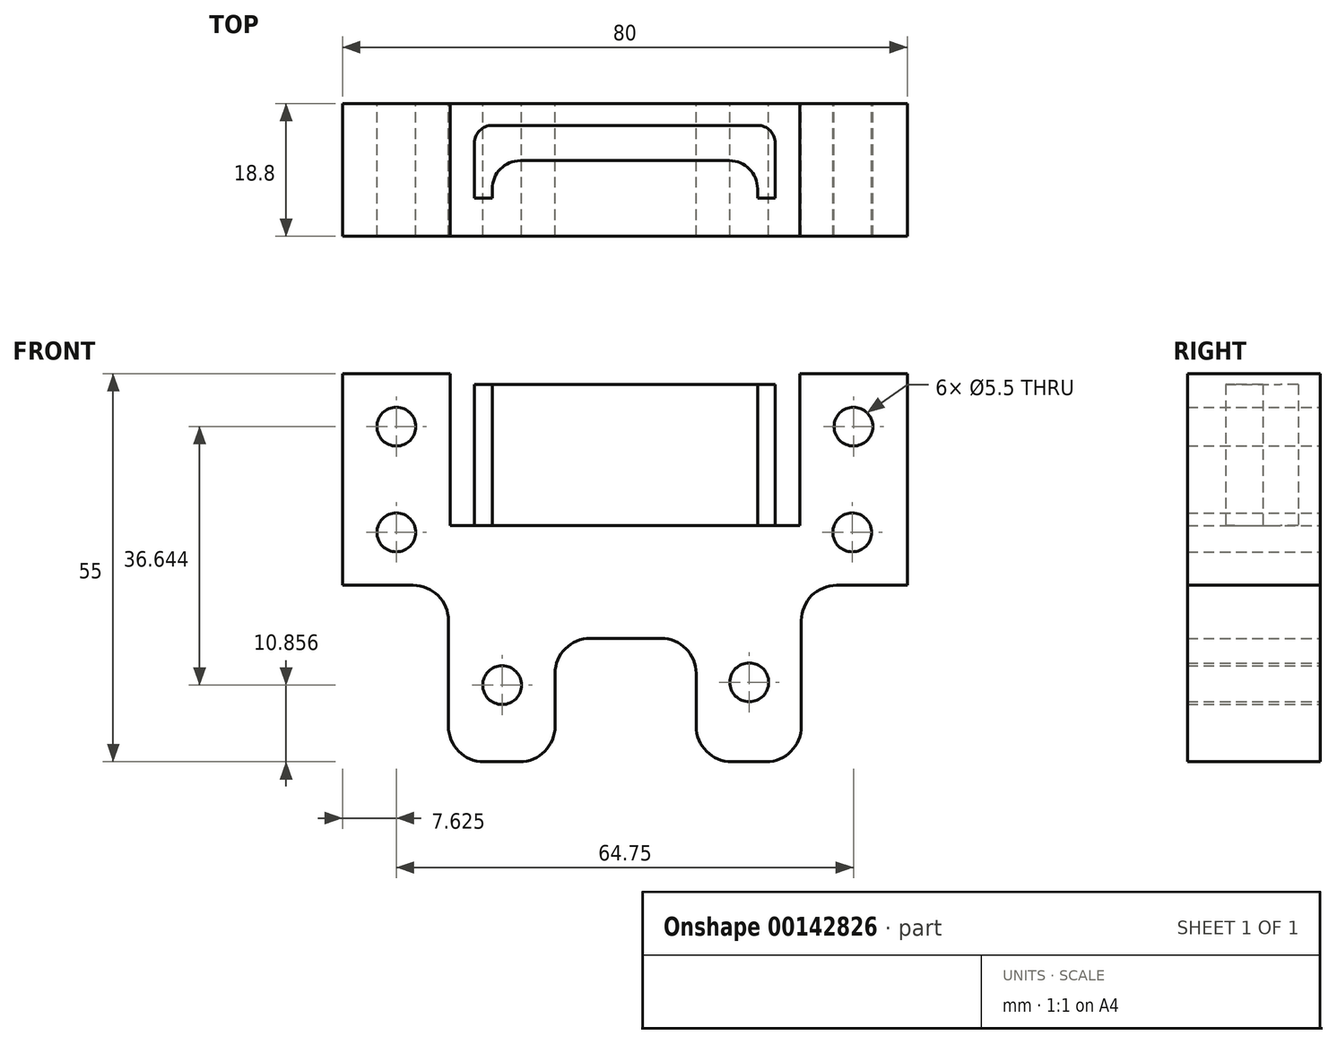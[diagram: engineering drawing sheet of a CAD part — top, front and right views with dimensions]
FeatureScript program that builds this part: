
annotation { "Feature Type Name" : "Feature", "Feature Type Description" : "" }
export const myFeature = defineFeature(function(context is Context, id is Id, definition is map)
    precondition{}
    {
        {
            var Q0;
            Q0=qCreatedBy(makeId("Front.planeOp"),FACE);
            var sketch = newSketch(context, id + "F0", { "sketchPlane" : qUnion([Q0])});
            skLineSegment(sketch, "E0.bottom", {"start": v(-40, 21.5) * mm, "end": v(-24.75, 21.5) * mm});
            skLineSegment(sketch, "E0.top", {"start": v(-25, -33.5) * mm, "end": v(-9.9, -33.5) * mm});
            skLineSegment(sketch, "E0.left", {"start": v(-40, 21.5) * mm, "end": v(-40, -8.5) * mm});
            skLineSegment(sketch, "E0.right", {"start": v(40, 21.5) * mm, "end": v(40, -8.5) * mm});
            skLineSegment(sketch, "E1.top", {"start": v(-24.75, 0) * mm, "end": v(24.75, 0) * mm});
            skLineSegment(sketch, "E1.left", {"start": v(-24.75, 21.5) * mm, "end": v(-24.75, 0) * mm});
            skLineSegment(sketch, "E1.right", {"start": v(24.75, 21.5) * mm, "end": v(24.75, 0) * mm});
            skLineSegment(sketch, "E2.trimOffspring", {"start": v(24.75, 21.5) * mm, "end": v(40, 21.5) * mm});
            skLineSegment(sketch, "E3", {"start": v(-25, -8.5) * mm, "end": v(-25, -33.5) * mm});
            skLineSegment(sketch, "E4", {"start": v(40, -8.5) * mm, "end": v(25, -8.5) * mm});
            skLineSegment(sketch, "E5", {"start": v(25, -8.5) * mm, "end": v(25, -33.5) * mm});
            skLineSegment(sketch, "E6", {"start": v(-40, -8.5) * mm, "end": v(-25, -8.5) * mm});
            skLineSegment(sketch, "E7.bottom", {"start": v(-9.9, -16) * mm, "end": v(10.1, -16) * mm});
            skLineSegment(sketch, "E7.left", {"start": v(-9.9, -16) * mm, "end": v(-9.9, -33.5) * mm});
            skLineSegment(sketch, "E7.right", {"start": v(10.1, -16) * mm, "end": v(10.1, -33.5) * mm});
            skLineSegment(sketch, "E8.trimOffspring", {"start": v(10.1, -33.5) * mm, "end": v(25, -33.5) * mm});
            skSolve(sketch);
        }
        {
            var Q0;
            Q0 = qSketchRegion(id + "F0", true);
            extrude(context, id + "F1", {"entities" : qUnion([Q0]), "depth" : 18.8 * mm, "offsetDistance" : 25 * mm});
        }
        {
            var Q0;
            Q0=makeQuery(id+"F1.opExtrude","SWEPT_FACE",FACE,{"disambiguationData":[OSD([sQuery(id+"F0.wireOp",EDGE,"E1.top")])]});
            var sketch = newSketch(context, id + "F2", { "sketchPlane" : qUnion([Q0])});
            skLineSegment(sketch, "E9.bottom", {"start": v(-21.3, -3.1) * mm, "end": v(21.3, -3.1) * mm});
            skLineSegment(sketch, "E10.0", {"start": v(-18.8, -8.1) * mm, "end": v(18.8, -8.1) * mm});
            skLineSegment(sketch, "E11.0", {"start": v(-21.3, -13.4) * mm, "end": v(-18.8, -13.4) * mm});
            skLineSegment(sketch, "E12", {"start": v(18.8, -8.1) * mm, "end": v(18.8, -13.4) * mm});
            skLineSegment(sketch, "E13.trimOffspring", {"start": v(18.8, -13.4) * mm, "end": v(21.3, -13.4) * mm});
            skPoint(sketch, "E14.orphan", {"position": v(-21.3, -15.9) * mm});
            skLineSegment(sketch, "E15", {"start": v(21.3, -13.4) * mm, "end": v(21.3, -3.1) * mm});
            skLineSegment(sketch, "E16", {"start": v(-21.3, -3.1) * mm, "end": v(-21.3, -13.4) * mm});
            skLineSegment(sketch, "E17", {"start": v(-18.8, -8.1) * mm, "end": v(-18.8, -13.4) * mm});
            skSolve(sketch);
        }
        {
            var Q0;
            Q0 = qSketchRegion(id + "F2", true);
            extrude(context, id + "F3", {"entities" : qUnion([Q0]), "depth" : 20 * mm, "offsetDistance" : 25 * mm});
        }
        {
            var Q0;
            Q0=makeQuery(id+"F3.opExtrude","SWEPT_EDGE",EDGE,{"disambiguationData":[OSD([sQuery(id+"F2.wireOp",EDGE,"E10.0"),sQuery(id+"F2.wireOp",EDGE,"E17")])]});
            fillet(context, id + "F4", {"entities" : qUnion([Q0]), "radius" : 4 * mm, "tangentPropagation" : true, "allowEdgeOverflow" : false});
        }
        {
            var Q0;
            Q0=makeQuery(id+"F3.opExtrude","SWEPT_EDGE",EDGE,{"disambiguationData":[OSD([sQuery(id+"F2.wireOp",EDGE,"E9.bottom"),sQuery(id+"F2.wireOp",EDGE,"E15")])]});
            fillet(context, id + "F5", {"entities" : qUnion([Q0]), "radius" : 2.5 * mm, "tangentPropagation" : true, "allowEdgeOverflow" : false});
        }
        {
            var Q0;
            Q0=makeQuery(id+"F3.opExtrude","SWEPT_EDGE",EDGE,{"disambiguationData":[OSD([sQuery(id+"F2.wireOp",EDGE,"E9.bottom"),sQuery(id+"F2.wireOp",EDGE,"E16")])]});
            fillet(context, id + "F6", {"entities" : qUnion([Q0]), "radius" : 2.5 * mm, "tangentPropagation" : true, "allowEdgeOverflow" : false});
        }
        {
            var Q0;
            Q0=makeQuery(id+"F3.opExtrude","SWEPT_EDGE",EDGE,{"disambiguationData":[OSD([sQuery(id+"F2.wireOp",EDGE,"E10.0"),sQuery(id+"F2.wireOp",EDGE,"E12")])]});
            fillet(context, id + "F7", {"entities" : qUnion([Q0]), "radius" : (4) * mm, "tangentPropagation" : true, "allowEdgeOverflow" : false});
        }
        {
            var Q0;
            Q0=makeQuery(id+"F1.opExtrude","SWEPT_EDGE",EDGE,{"disambiguationData":[OSD([sQuery(id+"F0.wireOp",EDGE,"E0.top"),sQuery(id+"F0.wireOp",EDGE,"E3")])]});
            var Q1;
            Q1=makeQuery(id+"F1.opExtrude","SWEPT_EDGE",EDGE,{"disambiguationData":[OSD([sQuery(id+"F0.wireOp",EDGE,"E0.top"),sQuery(id+"F0.wireOp",EDGE,"E7.left")])]});
            var Q2;
            Q2=makeQuery(id+"F1.opExtrude","SWEPT_EDGE",EDGE,{"disambiguationData":[OSD([sQuery(id+"F0.wireOp",EDGE,"E7.right"),sQuery(id+"F0.wireOp",EDGE,"E8.trimOffspring")])]});
            var Q3;
            Q3=makeQuery(id+"F1.opExtrude","SWEPT_EDGE",EDGE,{"disambiguationData":[OSD([sQuery(id+"F0.wireOp",EDGE,"E5"),sQuery(id+"F0.wireOp",EDGE,"E8.trimOffspring")])]});
            fillet(context, id + "F8", {"entities" : qUnion([Q0, Q1, Q2, Q3]), "radius" : 5 * mm, "tangentPropagation" : true, "allowEdgeOverflow" : false});
        }
        {
            var Q0;
            Q0=makeQuery(id+"F1.opExtrude","CAP_FACE",FACE,{"disambiguationData":[OSD([sQuery(id+"F0.wireOp",EDGE,"E0.bottom"),sQuery(id+"F0.wireOp",EDGE,"E0.top"),sQuery(id+"F0.wireOp",EDGE,"E0.left"),sQuery(id+"F0.wireOp",EDGE,"E0.right"),sQuery(id+"F0.wireOp",EDGE,"E1.top"),sQuery(id+"F0.wireOp",EDGE,"E1.left"),sQuery(id+"F0.wireOp",EDGE,"E1.right"),sQuery(id+"F0.wireOp",EDGE,"E2.trimOffspring"),sQuery(id+"F0.wireOp",EDGE,"E3"),sQuery(id+"F0.wireOp",EDGE,"E4"),sQuery(id+"F0.wireOp",EDGE,"E5"),sQuery(id+"F0.wireOp",EDGE,"E6"),sQuery(id+"F0.wireOp",EDGE,"E7.bottom"),sQuery(id+"F0.wireOp",EDGE,"E7.left"),sQuery(id+"F0.wireOp",EDGE,"E7.right"),sQuery(id+"F0.wireOp",EDGE,"E8.trimOffspring")])],"isStart":false});
            var sketch = newSketch(context, id + "F9", { "sketchPlane" : qUnion([Q0])});
            skPoint(sketch, "E18", {"position": v(-32.38, 14) * mm});
            skPoint(sketch, "E18.positionSnap0", {"position": v(-32.38, 21.5) * mm});
            skPoint(sketch, "E19", {"position": v(-32.38, -1) * mm});
            skPoint(sketch, "E20", {"position": v(-17.39, -22.64) * mm});
            skPoint(sketch, "E21", {"position": v(17.61, -22.25) * mm});
            skPoint(sketch, "E21.positionSnap0", {"position": v(10.1, -22.25) * mm});
            skPoint(sketch, "E22", {"position": v(32.38, 14) * mm});
            skPoint(sketch, "E22.positionSnap0", {"position": v(32.38, 21.5) * mm});
            skPoint(sketch, "E23", {"position": v(32.2, -1) * mm});
            skSolve(sketch);
        }
        {
            var Q0;
            Q0=makeQuery(id+"F1.opExtrude","SWEPT_EDGE",EDGE,{"disambiguationData":[OSD([sQuery(id+"F0.wireOp",EDGE,"E3"),sQuery(id+"F0.wireOp",EDGE,"E6")])]});
            fillet(context, id + "F10", {"entities" : qUnion([Q0]), "radius" : 5 * mm, "tangentPropagation" : true, "allowEdgeOverflow" : false});
        }
        {
            var Q0;
            Q0=makeQuery(id+"F1.opExtrude","SWEPT_EDGE",EDGE,{"disambiguationData":[OSD([sQuery(id+"F0.wireOp",EDGE,"E4"),sQuery(id+"F0.wireOp",EDGE,"E5")])]});
            fillet(context, id + "F11", {"entities" : qUnion([Q0]), "radius" : 5 * mm, "tangentPropagation" : true, "allowEdgeOverflow" : false});
        }
        {
            var Q0;
            Q0=makeQuery(id+"F1.opExtrude","SWEPT_EDGE",EDGE,{"disambiguationData":[OSD([sQuery(id+"F0.wireOp",EDGE,"E7.bottom"),sQuery(id+"F0.wireOp",EDGE,"E7.left")])]});
            var Q1;
            Q1=makeQuery(id+"F1.opExtrude","SWEPT_EDGE",EDGE,{"disambiguationData":[OSD([sQuery(id+"F0.wireOp",EDGE,"E7.bottom"),sQuery(id+"F0.wireOp",EDGE,"E7.right")])]});
            fillet(context, id + "F12", {"entities" : qUnion([Q0, Q1]), "radius" : 5 * mm, "tangentPropagation" : true, "allowEdgeOverflow" : false});
        }
        {
            var Q0;
            Q0=sQuery(id+"F9.wireOp",VERTEX,"E18");
            var Q1;
            Q1=sQuery(id+"F9.wireOp",VERTEX,"E19");
            var Q2;
            Q2=sQuery(id+"F9.wireOp",VERTEX,"E22");
            var Q3;
            Q3=sQuery(id+"F9.wireOp",VERTEX,"E23");
            var Q4;
            Q4=sQuery(id+"F9.wireOp",VERTEX,"E21");
            var Q5;
            Q5=sQuery(id+"F9.wireOp",VERTEX,"E20");
            var Q6;
            Q6=makeQuery(id+"F1.opExtrude","SWEPT_BODY",BODY,{"disambiguationData":[OSD([sQuery(id+"F0.wireOp",EDGE,"E0.bottom"),sQuery(id+"F0.wireOp",EDGE,"E0.top"),sQuery(id+"F0.wireOp",EDGE,"E0.left"),sQuery(id+"F0.wireOp",EDGE,"E0.right"),sQuery(id+"F0.wireOp",EDGE,"E1.top"),sQuery(id+"F0.wireOp",EDGE,"E1.left"),sQuery(id+"F0.wireOp",EDGE,"E1.right"),sQuery(id+"F0.wireOp",EDGE,"E2.trimOffspring"),sQuery(id+"F0.wireOp",EDGE,"E3"),sQuery(id+"F0.wireOp",EDGE,"E4"),sQuery(id+"F0.wireOp",EDGE,"E5"),sQuery(id+"F0.wireOp",EDGE,"E6"),sQuery(id+"F0.wireOp",EDGE,"E7.bottom"),sQuery(id+"F0.wireOp",EDGE,"E7.left"),sQuery(id+"F0.wireOp",EDGE,"E7.right"),sQuery(id+"F0.wireOp",EDGE,"E8.trimOffspring")])]});
            hole(context, id + "F13", {"style" : HoleStyle.SIMPLE, "endStyle" : HoleEndStyle.THROUGH, "holeDiameter" : 5.5 * mm, "majorDiameter" : 5 * mm, "isTappedThrough" : true, "tappedDepth" : 12 * mm, "tapClearance" : 3, "locations" : qUnion([Q0, Q1, Q2, Q3, Q4, Q5]), "scope" : qUnion([Q6]), "startStyle" : HoleStartStyle.SKETCH});
        }
    });
